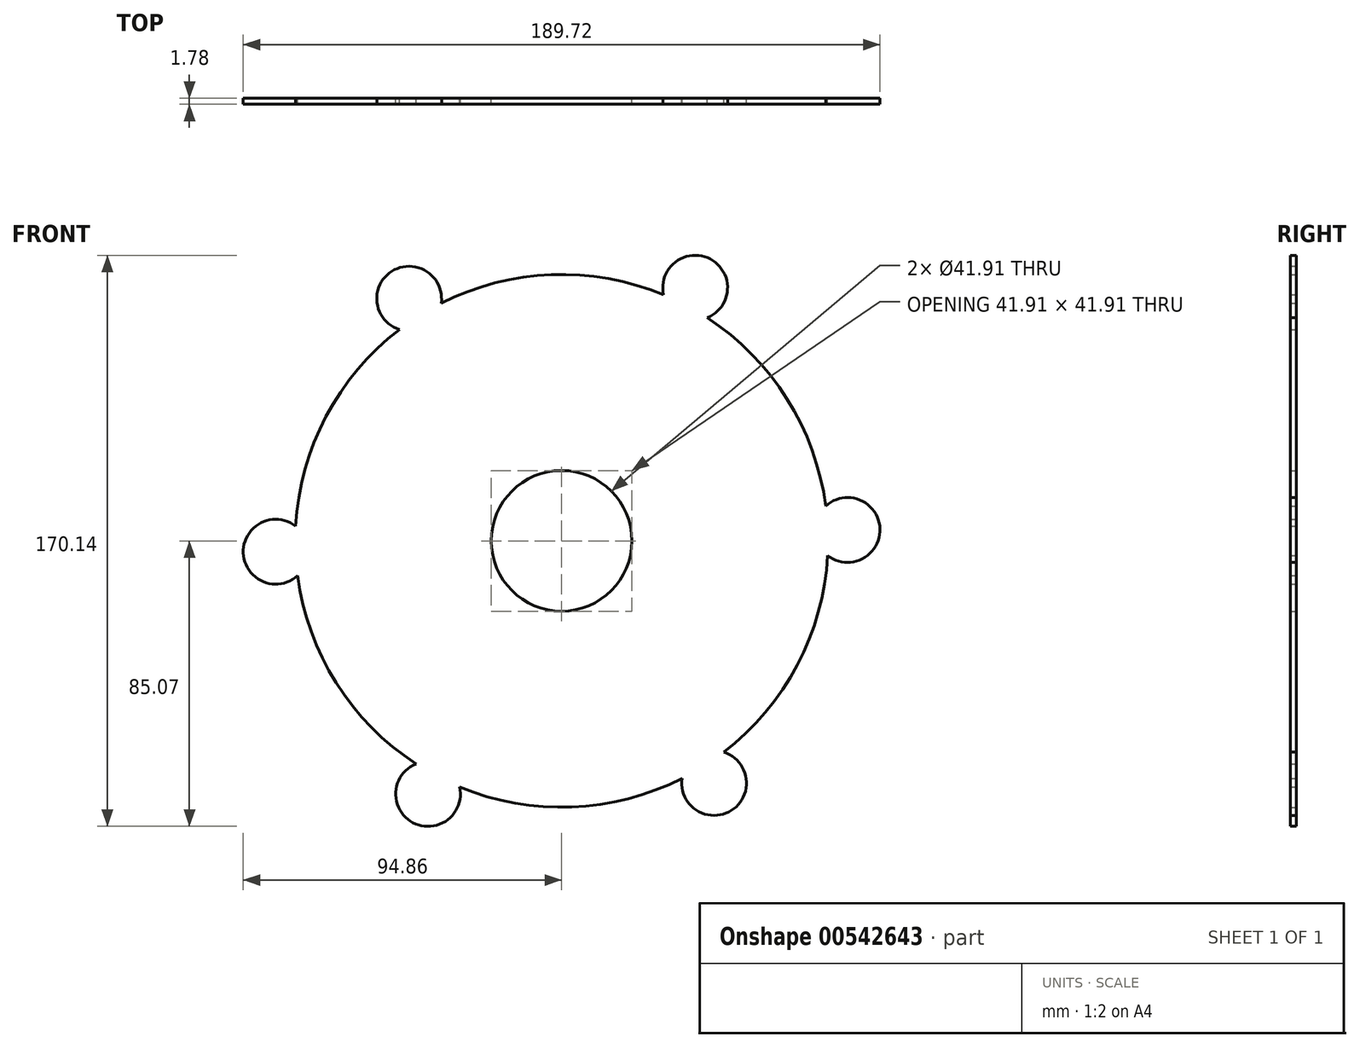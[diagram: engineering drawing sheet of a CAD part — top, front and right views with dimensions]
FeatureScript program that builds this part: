
annotation { "Feature Type Name" : "Feature", "Feature Type Description" : "" }
export const myFeature = defineFeature(function(context is Context, id is Id, definition is map)
    precondition{}
    {
        {
            var Q0;
            Q0=qCreatedBy(makeId("Front.planeOp"),FACE);
            var sketch = newSketch(context, id + "F0", { "sketchPlane" : qUnion([Q0])});
            skCircle(sketch, "E0", {"center": v(0, 0) * mm, "radius": 79.38 * mm});
            skArc(sketch, "E1", {"start": v(-79.26, 4.34) * mm, "mid": v(-94.86, -3.62) * mm, "end": v(-78.7, -10.37) * mm});
            skArc(sketch, "E2.1.0", {"start": v(-43.39, -66.47) * mm, "mid": v(-44.3, -83.96) * mm, "end": v(-30.36, -73.34) * mm});
            skArc(sketch, "E2.2.0", {"start": v(35.87, -70.8) * mm, "mid": v(50.56, -80.34) * mm, "end": v(48.33, -62.96) * mm});
            skArc(sketch, "E2.3.0", {"start": v(79.26, -4.34) * mm, "mid": v(94.86, 3.62) * mm, "end": v(78.7, 10.37) * mm});
            skArc(sketch, "E2.4.0", {"start": v(43.39, 66.47) * mm, "mid": v(44.3, 83.96) * mm, "end": v(30.36, 73.34) * mm});
            skArc(sketch, "E2.5.0", {"start": v(-35.87, 70.8) * mm, "mid": v(-50.56, 80.34) * mm, "end": v(-48.33, 62.96) * mm});
            skSolve(sketch);
        }
        {
            var Q0;
            {var subQ0=sQuery(id+"F0.wireOp",EDGE,"E2.2.0");Q0=makeQuery(id+"F0.imprint","IMPRINT",FACE,{"disambiguationData":[TD([[makeQuery(id+"F0.imprint","IMPRINT",EDGE,{"derivedFrom":subQ0}),1.0]])]});}
            var Q1;
            {var subQ0=sQuery(id+"F0.wireOp",EDGE,"E2.4.0");Q1=makeQuery(id+"F0.imprint","IMPRINT",FACE,{"disambiguationData":[TD([[makeQuery(id+"F0.imprint","IMPRINT",EDGE,{"derivedFrom":subQ0}),1.0]])]});}
            var Q2;
            {var subQ0=sQuery(id+"F0.wireOp",EDGE,"E2.5.0");Q2=makeQuery(id+"F0.imprint","IMPRINT",FACE,{"disambiguationData":[TD([[makeQuery(id+"F0.imprint","IMPRINT",EDGE,{"derivedFrom":subQ0}),1.0]])]});}
            var Q3;
            {var subQ0=sQuery(id+"F0.wireOp",EDGE,"E2.3.0");Q3=makeQuery(id+"F0.imprint","IMPRINT",FACE,{"disambiguationData":[TD([[makeQuery(id+"F0.imprint","IMPRINT",EDGE,{"derivedFrom":subQ0}),1.0]])]});}
            var Q4;
            {var subQ0=sQuery(id+"F0.wireOp",EDGE,"E2.1.0");Q4=makeQuery(id+"F0.imprint","IMPRINT",FACE,{"disambiguationData":[TD([[makeQuery(id+"F0.imprint","IMPRINT",EDGE,{"derivedFrom":subQ0}),1.0]])]});}
            var Q5;
            {var subQ1=sQuery(id+"F0.wireOp",EDGE,"E0");var subQ12=sQuery(id+"F0.wireOp",EDGE,"E2.3.0");var subQ13=makeQuery(id+"F0.imprint","INTERSECT",VERTEX,{"disambiguationData":[OD(1.0)],"derivedFrom":[subQ1,subQ12]});Q5=makeQuery(id+"F0.imprint","IMPRINT",FACE,{"disambiguationData":[TD([[makeQuery(id+"F0.imprint","IMPRINT",EDGE,{"disambiguationData":[TD([[subQ13,-1.0]])],"derivedFrom":subQ1}),1.0]])]});}
            var Q6;
            {var subQ0=sQuery(id+"F0.wireOp",EDGE,"E1");Q6=makeQuery(id+"F0.imprint","IMPRINT",FACE,{"disambiguationData":[TD([[makeQuery(id+"F0.imprint","IMPRINT",EDGE,{"derivedFrom":subQ0}),1.0]])]});}
            extrude(context, id + "F1", {"entities" : qUnion([Q0, Q1, Q2, Q3, Q4, Q5, Q6]), "depth" : 1.78 * mm, "offsetDistance" : 25.4 * mm});
        }
        {
            var Q0;
            Q0=sQuery(id+"F0.wireOp",VERTEX,"E0.center");
            var Q1;
            Q1=makeQuery(id+"F1.opExtrude","SWEPT_BODY",BODY,{"disambiguationData":[OSD([sQuery(id+"F0.wireOp",EDGE,"E0"),sQuery(id+"F0.wireOp",EDGE,"E1"),sQuery(id+"F0.wireOp",EDGE,"E2.1.0"),sQuery(id+"F0.wireOp",EDGE,"E2.2.0"),sQuery(id+"F0.wireOp",EDGE,"E2.3.0"),sQuery(id+"F0.wireOp",EDGE,"E2.4.0"),sQuery(id+"F0.wireOp",EDGE,"E2.5.0")])]});
            hole(context, id + "F2", {"style" : HoleStyle.SIMPLE, "endStyle" : HoleEndStyle.THROUGH, "oppositeDirection" : true, "holeDiameter" : 41.9 * mm, "isTappedThrough" : true, "tappedDepth" : 12.7 * mm, "tapClearance" : 3, "locations" : qUnion([Q0]), "scope" : qUnion([Q1])});
        }
    });
